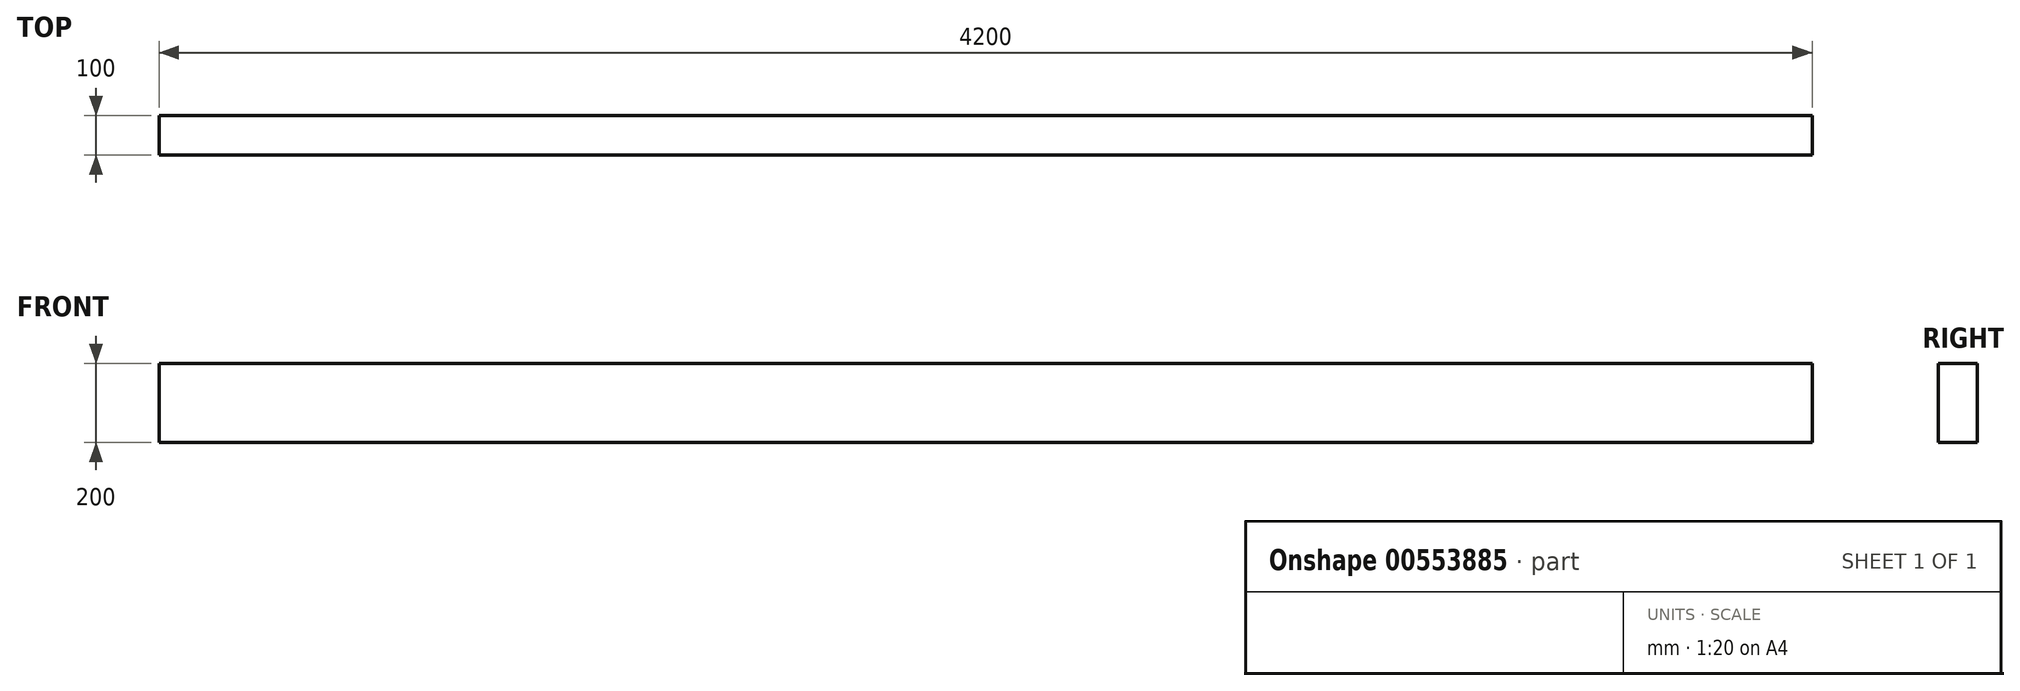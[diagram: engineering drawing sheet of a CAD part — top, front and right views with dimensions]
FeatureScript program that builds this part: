
annotation { "Feature Type Name" : "Feature", "Feature Type Description" : "" }
export const myFeature = defineFeature(function(context is Context, id is Id, definition is map)
    precondition{}
    {
        {
            var Q0;
            Q0=qCreatedBy(makeId("Top.planeOp"),FACE);
            var sketch = newSketch(context, id + "F0", { "sketchPlane" : qUnion([Q0])});
            skLineSegment(sketch, "E0.bottom", {"start": v(-2047.38, -21.46) * mm, "end": v(2152.62, -21.46) * mm});
            skLineSegment(sketch, "E0.top", {"start": v(-2047.38, -121.46) * mm, "end": v(2152.62, -121.46) * mm});
            skLineSegment(sketch, "E0.left", {"start": v(-2047.38, -21.46) * mm, "end": v(-2047.38, -121.46) * mm});
            skLineSegment(sketch, "E0.right", {"start": v(2152.62, -21.46) * mm, "end": v(2152.62, -121.46) * mm});
            skSolve(sketch);
        }
        {
            var Q0;
            Q0=makeQuery(id+"F0.imprint","IMPRINT",FACE,{"disambiguationData":[TD([[makeQuery(id+"F0.imprint","IMPRINT",EDGE,{"derivedFrom":sQuery(id+"F0.wireOp",EDGE,"E0.bottom")}),-1.0]])]});
            extrude(context, id + "F1", {"entities" : qUnion([Q0]), "depth" : 200 * mm});
        }
    });
